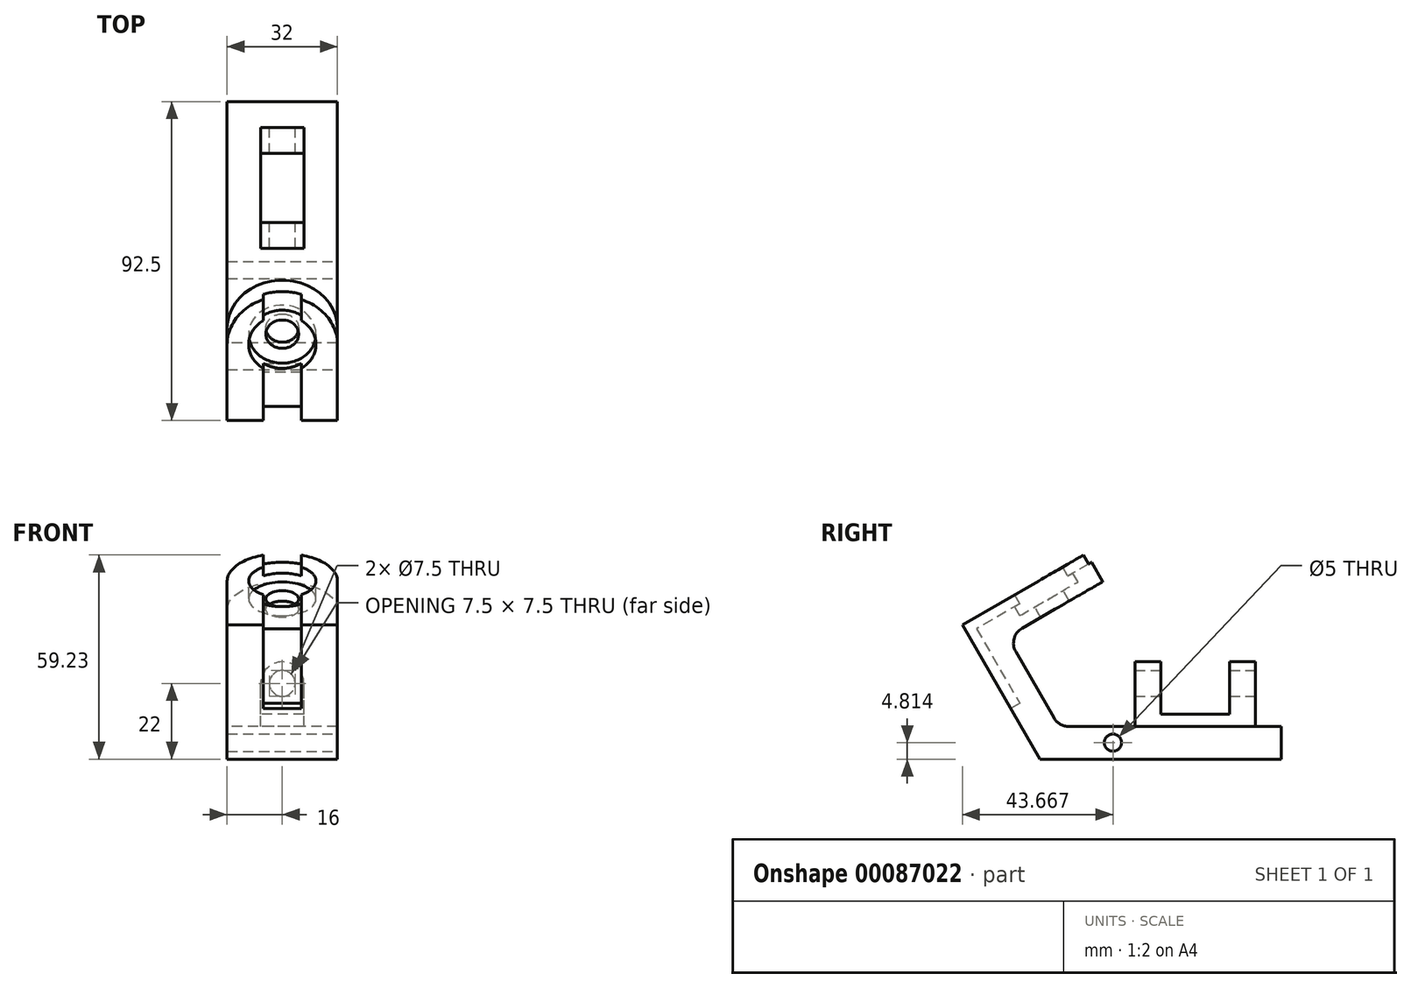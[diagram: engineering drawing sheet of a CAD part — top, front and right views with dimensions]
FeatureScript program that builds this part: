
annotation { "Feature Type Name" : "Feature", "Feature Type Description" : "" }
export const myFeature = defineFeature(function(context is Context, id is Id, definition is map)
    precondition{}
    {
        {
            var Q0;
            Q0=qCreatedBy(makeId("Right.planeOp"),FACE);
            var sketch = newSketch(context, id + "F0", { "sketchPlane" : qUnion([Q0])});
            skLineSegment(sketch, "E0", {"start": v(0, 0) * mm, "end": v(-140, 0) * mm});
            skLineSegment(sketch, "E1", {"start": v(-140, 0) * mm, "end": v(-185, 77.94) * mm});
            skLineSegment(sketch, "E2", {"start": v(-185, 77.94) * mm, "end": v(-140.83, 103.44) * mm});
            skLineSegment(sketch, "E3", {"start": v(-140.83, 103.44) * mm, "end": v(-131.33, 86.99) * mm});
            skLineSegment(sketch, "E4", {"start": v(-131.33, 86.99) * mm, "end": v(-159.05, 70.99) * mm});
            skLineSegment(sketch, "E5", {"start": v(-159.05, 70.99) * mm, "end": v(-129.03, 19) * mm});
            skLineSegment(sketch, "E6", {"start": v(-129.03, 19) * mm, "end": v(0, 19) * mm});
            skLineSegment(sketch, "E7", {"start": v(0, 19) * mm, "end": v(0, 0) * mm});
            skSolve(sketch);
        }
        {
            var Q0;
            Q0=makeQuery(id+"F0.imprint","IMPRINT",FACE,{"disambiguationData":[TD([[makeQuery(id+"F0.imprint","IMPRINT",EDGE,{"derivedFrom":sQuery(id+"F0.wireOp",EDGE,"E0")}),-1.0]])]});
            extrude(context, id + "F1", {"entities" : qUnion([Q0]), "endBound" : BoundingType.SYMMETRIC, "depth" : 64 * mm});
        }
        {
            var Q0;
            Q0=makeQuery(id+"F1.opExtrude","SWEPT_FACE",FACE,{"disambiguationData":[OSD([sQuery(id+"F0.wireOp",EDGE,"E2")])]});
            var sketch = newSketch(context, id + "F2", { "sketchPlane" : qUnion([Q0])});
            skCircle(sketch, "E8", {"center": v(0, -70.24) * mm, "radius": 32 * mm});
            skSolve(sketch);
        }
        {
            var Q0;
            Q0 = qSketchRegion(id + "F2", true);
            var Q1;
            Q1=makeQuery(id+"F1.opExtrude","SWEPT_FACE",FACE,{"disambiguationData":[OSD([sQuery(id+"F0.wireOp",EDGE,"E4")])]});
            extrude(context, id + "F3", {"entities" : qUnion([Q0]), "operationType" : NewBodyOperationType.ADD, "endBound" : BoundingType.UP_TO_SURFACE, "oppositeDirection" : true, "endBoundEntityFace" : qUnion([Q1]), "depth" : 25 * mm});
        }
        {
            var Q0;
            Q0=makeQuery(id+"F3.boolean.opBoolean","MERGE",FACE,{"derivedFrom":[makeQuery(id+"F1.opExtrude","SWEPT_FACE",FACE,{"disambiguationData":[OSD([sQuery(id+"F0.wireOp",EDGE,"E2")])]}),makeQuery(id+"F3.opExtrude","CAP_FACE",FACE,{"disambiguationData":[OSD([sQuery(id+"F2.wireOp",EDGE,"E8")])],"isStart":true})]});
            var sketch = newSketch(context, id + "F4", { "sketchPlane" : qUnion([Q0])});
            skCircle(sketch, "E9", {"center": v(0, -70.24) * mm, "radius": 9.5 * mm});
            skSolve(sketch);
        }
        {
            var Q0;
            Q0 = qSketchRegion(id + "F4", true);
            var Q1;
            Q1=makeQuery(id+"F3.boolean.opBoolean","MERGE",FACE,{"derivedFrom":[makeQuery(id+"F1.opExtrude","SWEPT_FACE",FACE,{"disambiguationData":[OSD([sQuery(id+"F0.wireOp",EDGE,"E4")])]}),makeQuery(id+"F3.opExtrude","CAP_FACE",FACE,{"disambiguationData":[OSD([sQuery(id+"F2.wireOp",EDGE,"E8")])],"isStart":false})]});
            extrude(context, id + "F5", {"entities" : qUnion([Q0]), "operationType" : NewBodyOperationType.REMOVE, "endBound" : BoundingType.UP_TO_SURFACE, "oppositeDirection" : true, "endBoundEntityFace" : qUnion([Q1]), "depth" : 25 * mm});
        }
        {
            var Q0;
            Q0=makeQuery(id+"F3.boolean.opBoolean","MERGE",FACE,{"derivedFrom":[makeQuery(id+"F1.opExtrude","SWEPT_FACE",FACE,{"disambiguationData":[OSD([sQuery(id+"F0.wireOp",EDGE,"E2")])]}),makeQuery(id+"F3.opExtrude","CAP_FACE",FACE,{"disambiguationData":[OSD([sQuery(id+"F2.wireOp",EDGE,"E8")])],"isStart":true})]});
            var sketch = newSketch(context, id + "F6", { "sketchPlane" : qUnion([Q0])});
            skCircle(sketch, "E10", {"center": v(0, -70.24) * mm, "radius": 19.5 * mm});
            skSolve(sketch);
        }
        {
            var Q0;
            Q0=makeQuery(id+"F6.imprint","IMPRINT",FACE,{"disambiguationData":[TD([[makeQuery(id+"F6.imprint","IMPRINT",EDGE,{"derivedFrom":sQuery(id+"F6.wireOp",EDGE,"E10")}),1.0]])]});
            extrude(context, id + "F7", {"entities" : qUnion([Q0]), "operationType" : NewBodyOperationType.REMOVE, "oppositeDirection" : true, "depth" : 12 * mm});
        }
        {
            var Q0;
            Q0=qCreatedBy(makeId("Right.planeOp"),FACE);
            var sketch = newSketch(context, id + "F8", { "sketchPlane" : qUnion([Q0])});
            skLineSegment(sketch, "E11", {"start": v(-102.42, 118.7) * mm, "end": v(-176.8, 75.75) * mm});
            skLineSegment(sketch, "E12", {"start": v(-176.8, 75.75) * mm, "end": v(-151.8, 32.44) * mm});
            skLineSegment(sketch, "E13", {"start": v(-151.8, 32.44) * mm, "end": v(-158.47, 28.6) * mm});
            skLineSegment(sketch, "E14", {"start": v(-102.42, 118.7) * mm, "end": v(-139.85, 145.45) * mm});
            skLineSegment(sketch, "E15", {"start": v(-139.85, 145.45) * mm, "end": v(-219.75, 72.32) * mm});
            skLineSegment(sketch, "E16", {"start": v(-219.75, 72.32) * mm, "end": v(-158.47, 28.6) * mm});
            skSolve(sketch);
        }
        {
            var Q0;
            Q0 = qSketchRegion(id + "F8", true);
            extrude(context, id + "F9", {"entities" : qUnion([Q0]), "operationType" : NewBodyOperationType.REMOVE, "endBound" : BoundingType.SYMMETRIC, "oppositeDirection" : true, "depth" : 22 * mm});
        }
        {
            var Q0;
            Q0=makeQuery(id+"F1.opExtrude","SWEPT_EDGE",EDGE,{"disambiguationData":[OSD([sQuery(id+"F0.wireOp",EDGE,"E4"),sQuery(id+"F0.wireOp",EDGE,"E5")])]});
            var Q1;
            Q1=makeQuery(id+"F1.opExtrude","SWEPT_EDGE",EDGE,{"disambiguationData":[OSD([sQuery(id+"F0.wireOp",EDGE,"E5"),sQuery(id+"F0.wireOp",EDGE,"E6")])]});
            fillet(context, id + "F10", {"entities" : qUnion([Q0, Q1]), "radius" : 10 * mm, "tangentPropagation" : true, "allowEdgeOverflow" : false});
        }
        {
            var Q0;
            Q0=qCreatedBy(makeId("Right.planeOp"),FACE);
            var sketch = newSketch(context, id + "F11", { "sketchPlane" : qUnion([Q0])});
            skLineSegment(sketch, "E17.0", {"start": v(-123.26, 19) * mm, "end": v(0, 19) * mm});
            skLineSegment(sketch, "E18", {"start": v(-85, 19) * mm, "end": v(-85, 44) * mm});
            skLineSegment(sketch, "E19", {"start": v(-85, 44) * mm, "end": v(-70, 44) * mm});
            skLineSegment(sketch, "E20", {"start": v(-70, 44) * mm, "end": v(-70, 26) * mm});
            skLineSegment(sketch, "E21", {"start": v(-70, 26) * mm, "end": v(-30, 26) * mm});
            skLineSegment(sketch, "E22", {"start": v(-30, 26) * mm, "end": v(-30, 44) * mm});
            skLineSegment(sketch, "E23", {"start": v(-30, 44) * mm, "end": v(-15, 44) * mm});
            skLineSegment(sketch, "E24", {"start": v(-15, 44) * mm, "end": v(-15, 19) * mm});
            skSolve(sketch);
        }
        {
            var Q0;
            Q0 = qSketchRegion(id + "F11", true);
            extrude(context, id + "F12", {"entities" : qUnion([Q0]), "operationType" : NewBodyOperationType.ADD, "endBound" : BoundingType.SYMMETRIC, "depth" : 25 * mm});
        }
        {
            var Q0;
            Q0=makeQuery(id+"F12.opExtrude","SWEPT_FACE",FACE,{"disambiguationData":[OSD([sQuery(id+"F11.wireOp",EDGE,"E18")])]});
            var sketch = newSketch(context, id + "F13", { "sketchPlane" : qUnion([Q0])});
            skCircle(sketch, "E25", {"center": v(0, 44) * mm, "radius": 12.5 * mm});
            skSolve(sketch);
        }
        {
            var Q0;
            Q0 = qSketchRegion(id + "F13", true);
            var Q1;
            Q1=makeQuery(id+"F12.opExtrude","SWEPT_FACE",FACE,{"disambiguationData":[OSD([sQuery(id+"F11.wireOp",EDGE,"E20")])]});
            extrude(context, id + "F14", {"entities" : qUnion([Q0]), "operationType" : NewBodyOperationType.ADD, "endBound" : BoundingType.UP_TO_SURFACE, "oppositeDirection" : true, "endBoundEntityFace" : qUnion([Q1]), "depth" : 25 * mm});
        }
        {
            var Q0;
            Q0=makeQuery(id+"F12.opExtrude","SWEPT_FACE",FACE,{"disambiguationData":[OSD([sQuery(id+"F11.wireOp",EDGE,"E22")])]});
            var sketch = newSketch(context, id + "F15", { "sketchPlane" : qUnion([Q0])});
            skCircle(sketch, "E26", {"center": v(0, 44) * mm, "radius": 12.5 * mm});
            skSolve(sketch);
        }
        {
            var Q0;
            Q0 = qSketchRegion(id + "F15", true);
            var Q1;
            Q1=makeQuery(id+"F12.opExtrude","SWEPT_FACE",FACE,{"disambiguationData":[OSD([sQuery(id+"F11.wireOp",EDGE,"E24")])]});
            extrude(context, id + "F16", {"entities" : qUnion([Q0]), "operationType" : NewBodyOperationType.ADD, "endBound" : BoundingType.UP_TO_SURFACE, "oppositeDirection" : true, "endBoundEntityFace" : qUnion([Q1]), "depth" : 25 * mm});
        }
        {
            var Q0;
            Q0=makeQuery(id+"F16.boolean.opBoolean","MERGE",FACE,{"derivedFrom":[makeQuery(id+"F12.opExtrude","SWEPT_FACE",FACE,{"disambiguationData":[OSD([sQuery(id+"F11.wireOp",EDGE,"E24")])]}),makeQuery(id+"F16.opExtrude","CAP_FACE",FACE,{"disambiguationData":[OSD([sQuery(id+"F15.wireOp",EDGE,"E26")])],"isStart":false})]});
            var sketch = newSketch(context, id + "F17", { "sketchPlane" : qUnion([Q0])});
            skCircle(sketch, "E27", {"center": v(0, 44) * mm, "radius": 7.5 * mm});
            skSolve(sketch);
        }
        {
            var Q0;
            Q0 = qSketchRegion(id + "F17", true);
            var Q1;
            Q1=makeQuery(id+"F14.boolean.opBoolean","MERGE",FACE,{"derivedFrom":[makeQuery(id+"F12.opExtrude","SWEPT_FACE",FACE,{"disambiguationData":[OSD([sQuery(id+"F11.wireOp",EDGE,"E18")])]}),makeQuery(id+"F14.opExtrude","CAP_FACE",FACE,{"disambiguationData":[OSD([sQuery(id+"F13.wireOp",EDGE,"E25")])],"isStart":true})]});
            extrude(context, id + "F18", {"entities" : qUnion([Q0]), "operationType" : NewBodyOperationType.REMOVE, "endBound" : BoundingType.UP_TO_SURFACE, "oppositeDirection" : true, "endBoundEntityFace" : qUnion([Q1]), "depth" : 25 * mm});
        }
        {
            var Q0;
            Q0=makeQuery(id+"F1.opExtrude","CAP_FACE",FACE,{"disambiguationData":[OSD([sQuery(id+"F0.wireOp",EDGE,"E0"),sQuery(id+"F0.wireOp",EDGE,"E1"),sQuery(id+"F0.wireOp",EDGE,"E2"),sQuery(id+"F0.wireOp",EDGE,"E3"),sQuery(id+"F0.wireOp",EDGE,"E4"),sQuery(id+"F0.wireOp",EDGE,"E5"),sQuery(id+"F0.wireOp",EDGE,"E6"),sQuery(id+"F0.wireOp",EDGE,"E7")])],"isStart":false});
            var sketch = newSketch(context, id + "F19", { "sketchPlane" : qUnion([Q0])});
            skPoint(sketch, "E28", {"position": v(-97.67, 9.63) * mm});
            skSolve(sketch);
        }
        {
            var Q0;
            Q0=sQuery(id+"F19.wireOp",VERTEX,"E28");
            var Q1;
            Q1=makeQuery(id+"F1.opExtrude","SWEPT_BODY",BODY,{"disambiguationData":[OSD([sQuery(id+"F0.wireOp",EDGE,"E0"),sQuery(id+"F0.wireOp",EDGE,"E1"),sQuery(id+"F0.wireOp",EDGE,"E2"),sQuery(id+"F0.wireOp",EDGE,"E3"),sQuery(id+"F0.wireOp",EDGE,"E4"),sQuery(id+"F0.wireOp",EDGE,"E5"),sQuery(id+"F0.wireOp",EDGE,"E6"),sQuery(id+"F0.wireOp",EDGE,"E7")])]});
            hole(context, id + "F20", {"style" : HoleStyle.SIMPLE, "endStyle" : HoleEndStyle.THROUGH, "holeDiameter" : 10 * mm, "locations" : qUnion([Q0]), "scope" : qUnion([Q1]), "isTappedThrough" : true});
        }
        {
            var Q0;
            Q0=makeQuery(id+"F1.opExtrude","SWEPT_BODY",BODY,{"disambiguationData":[OSD([sQuery(id+"F0.wireOp",EDGE,"E0"),sQuery(id+"F0.wireOp",EDGE,"E1"),sQuery(id+"F0.wireOp",EDGE,"E2"),sQuery(id+"F0.wireOp",EDGE,"E3"),sQuery(id+"F0.wireOp",EDGE,"E4"),sQuery(id+"F0.wireOp",EDGE,"E5"),sQuery(id+"F0.wireOp",EDGE,"E6"),sQuery(id+"F0.wireOp",EDGE,"E7")])]});
            var Q1;
            Q1=qCreatedBy(makeId("Origin.pointOp"),VERTEX);
            transform(context, id + "F21", {"entities" : qUnion([Q0]), "transformType" : TransformType.SCALE_UNIFORMLY, "scale" : .5, "scalePoint" : qUnion([Q1]), "makeCopy" : false});
        }
    });
